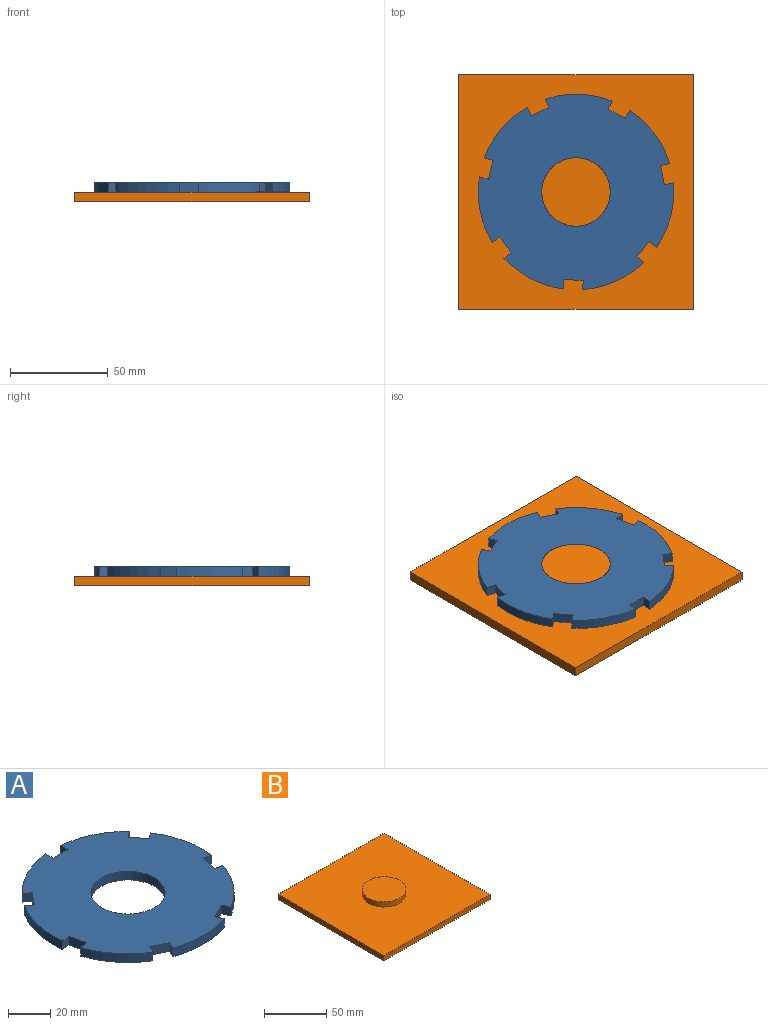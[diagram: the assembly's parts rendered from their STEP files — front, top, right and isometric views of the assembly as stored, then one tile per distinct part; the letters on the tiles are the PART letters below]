
ASSEMBLY  parts=2 mates=1
PART A: 31 faces, bbox 100x99.7x5 mm
  f0: cylinder r=50mm len=30.78mm, axis (0,0,-1), area 174.3mm2, adj f2,f25,f26,f30
  f1: plane 5x3.71mm, normal (-0.62,0.78,0), area 23.7mm2, adj f3,f4,f25,f26
  f2: plane 5x3.71mm, normal (0.62,-0.78,0), area 23.7mm2, adj f0,f3,f25,f26
  f3: plane 7.82x6.24mm, normal (0.78,0.62,0), area 50mm2, adj f1,f2,f25,f26
  f4: cylinder r=50mm len=33.3mm, axis (0,0,-1), area 174.3mm2, adj f1,f6,f25,f26
  f5: plane 5x4.63mm, normal (0.22,0.97,0), area 23.7mm2, adj f7,f8,f25,f26
  f6: plane 5x4.63mm, normal (-0.22,-0.97,0), area 23.7mm2, adj f4,f7,f25,f26
  f7: plane 9.75x5mm, normal (0.97,-0.22,0), area 50mm2, adj f5,f6,f25,f26
  f8: cylinder r=50mm len=26.71mm, axis (0,0,-1), area 174.3mm2, adj f5,f10,f25,f26
  f9: plane 5x4.28mm, normal (0.9,0.43,0), area 23.7mm2, adj f11,f12,f25,f26
  f10: plane 5x4.28mm, normal (-0.9,-0.43,0), area 23.7mm2, adj f8,f11,f25,f26
  f11: plane 9.01x5mm, normal (0.43,-0.9,0), area 50mm2, adj f9,f10,f25,f26
  f12: cylinder r=50mm len=34.16mm, axis (0,0,-1), area 174.3mm2, adj f9,f14,f25,f26
  f13: plane 5x4.28mm, normal (0.9,-0.43,0), area 23.7mm2, adj f15,f16,f25,f26
  f14: plane 5x4.28mm, normal (-0.9,0.43,0), area 23.7mm2, adj f12,f15,f25,f26
  f15: plane 9.01x5mm, normal (-0.43,-0.9,0), area 50mm2, adj f13,f14,f25,f26
  f16: cylinder r=50mm len=26.71mm, axis (0,0,-1), area 174.3mm2, adj f13,f18,f25,f26
  f17: plane 5x4.63mm, normal (0.22,-0.97,0), area 23.7mm2, adj f19,f20,f25,f26
  f18: plane 5x4.63mm, normal (-0.22,0.97,0), area 23.7mm2, adj f16,f19,f25,f26
  f19: plane 9.75x5mm, normal (-0.97,-0.22,0), area 50mm2, adj f17,f18,f25,f26
  f20: cylinder r=50mm len=33.3mm, axis (0,0,-1), area 174.3mm2, adj f17,f22,f25,f26
  f21: plane 5x3.71mm, normal (-0.62,-0.78,0), area 23.7mm2, adj f23,f24,f25,f26
  f22: plane 5x3.71mm, normal (0.62,0.78,0), area 23.7mm2, adj f20,f23,f25,f26
  f23: plane 7.82x6.24mm, normal (-0.78,0.62,0), area 50mm2, adj f21,f22,f25,f26
  f24: cylinder r=50mm len=30.78mm, axis (0,0,-1), area 174.3mm2, adj f21,f25,f26,f28
  f25: plane 100x99.75mm, normal (0,0,1), area 6547.7mm2, adj f0,f1,f2,f3,f4,f5,f6,f7
  f26: plane 100x99.75mm, normal (0,0,-1), area 6547.7mm2, adj f0,f1,f2,f3,f4,f5,f6,f7
  f27: cylinder r=17.5mm len=35mm, axis (0,0,1), area 549.8mm2, adj f25,f26
  f28: plane 5x4.75mm, normal (1,0,0), area 23.7mm2, adj f24,f25,f26,f29
  f29: plane 10x5mm, normal (0,1,0), area 50mm2, adj f25,f26,f28,f30
  f30: plane 5x4.75mm, normal (-1,0,0), area 23.7mm2, adj f0,f25,f26,f29
PART B: 8 faces, bbox 120x120x10 mm
  f0: plane 120x5mm, normal (1,0,0), area 600mm2, adj f1,f3,f4,f5
  f1: plane 120x5mm, normal (0,1,0), area 600mm2, adj f0,f2,f4,f5
  f2: plane 120x5mm, normal (-1,0,0), area 600mm2, adj f1,f3,f4,f5
  f3: plane 120x5mm, normal (0,-1,0), area 600mm2, adj f0,f2,f4,f5
  f4: plane 120x120mm, normal (0,0,1), area 13437.9mm2, adj f0,f1,f2,f3,f6
  f5: plane 120x120mm, normal (0,0,-1), area 14400mm2, adj f0,f1,f2,f3
  f6: cylinder r=17.5mm len=35mm, axis (0,0,-1), area 549.8mm2, adj f4,f7
  f7: plane 35x35mm, normal (0,0,1), area 962.1mm2, adj f6
PLACE A rot(axis=(0,0,1),75.4deg) t=(0.02,9.38,2.36)mm
PLACE B t=(0.02,9.38,-2.64)mm fixed
MATE revolute A.f27 <-> B.f6  axis (0,0,-1) through (0.02,9.38,2.36)mm
